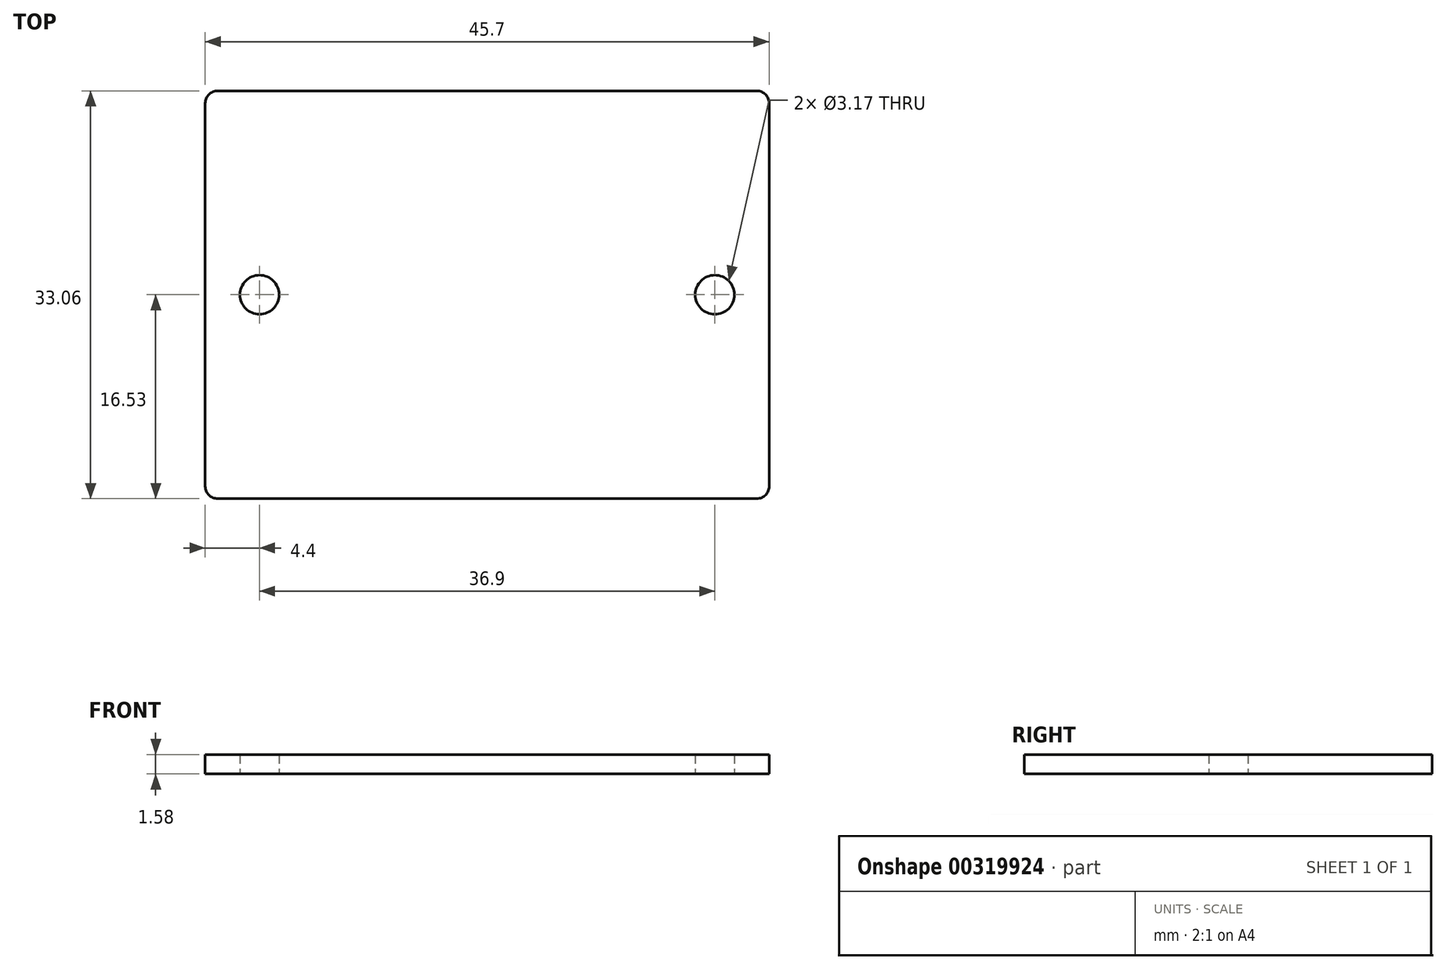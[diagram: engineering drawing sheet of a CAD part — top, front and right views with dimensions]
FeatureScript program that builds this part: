
annotation { "Feature Type Name" : "Feature", "Feature Type Description" : "" }
export const myFeature = defineFeature(function(context is Context, id is Id, definition is map)
    precondition{}
    {
        {
            var Q0;
            Q0=qCreatedBy(makeId("Top.planeOp"),FACE);
            var sketch = newSketch(context, id + "F0", { "sketchPlane" : qUnion([Q0])});
            skLineSegment(sketch, "E0.bottom", {"start": v(21.85, -16.53) * mm, "end": v(-21.85, -16.53) * mm});
            skLineSegment(sketch, "E0.top", {"start": v(21.85, 16.53) * mm, "end": v(-21.85, 16.53) * mm});
            skLineSegment(sketch, "E0.left", {"start": v(22.85, -15.53) * mm, "end": v(22.85, 15.53) * mm});
            skLineSegment(sketch, "E0.right", {"start": v(-22.85, -15.53) * mm, "end": v(-22.85, 15.53) * mm});
            skPoint(sketch, "E0.middle", {"position": v(0, 0) * mm});
            skCircle(sketch, "E1", {"center": v(-18.45, 0) * mm, "radius": 1.59 * mm});
            skCircle(sketch, "E2.MirrorC", {"center": v(18.45, 0) * mm, "radius": 1.59 * mm});
            skPoint(sketch, "E3.visualSharp", {"position": v(-22.85, 16.53) * mm});
            skArc(sketch, "E3.filletArc", {"start": v(-21.85, 16.53) * mm, "mid": v(-22.56, 16.24) * mm, "end": v(-22.85, 15.53) * mm});
            skPoint(sketch, "E4.visualSharp", {"position": v(22.85, 16.53) * mm});
            skArc(sketch, "E4.filletArc", {"start": v(22.85, 15.53) * mm, "mid": v(22.56, 16.24) * mm, "end": v(21.85, 16.53) * mm});
            skPoint(sketch, "E5.visualSharp", {"position": v(-22.85, -16.53) * mm});
            skArc(sketch, "E5.filletArc", {"start": v(-22.85, -15.53) * mm, "mid": v(-22.56, -16.24) * mm, "end": v(-21.85, -16.53) * mm});
            skPoint(sketch, "E6.visualSharp", {"position": v(22.85, -16.53) * mm});
            skArc(sketch, "E6.filletArc", {"start": v(21.85, -16.53) * mm, "mid": v(22.56, -16.24) * mm, "end": v(22.85, -15.53) * mm});
            skSolve(sketch);
        }
        {
            var Q0;
            Q0=makeQuery(id+"F0.imprint","IMPRINT",FACE,{"disambiguationData":[TD([[makeQuery(id+"F0.imprint","IMPRINT",EDGE,{"derivedFrom":sQuery(id+"F0.wireOp",EDGE,"E0.bottom")}),-1.0]])]});
            extrude(context, id + "F1", {"entities" : qUnion([Q0]), "depth" : 1.57 * mm, "symmetric" : true});
        }
    });
